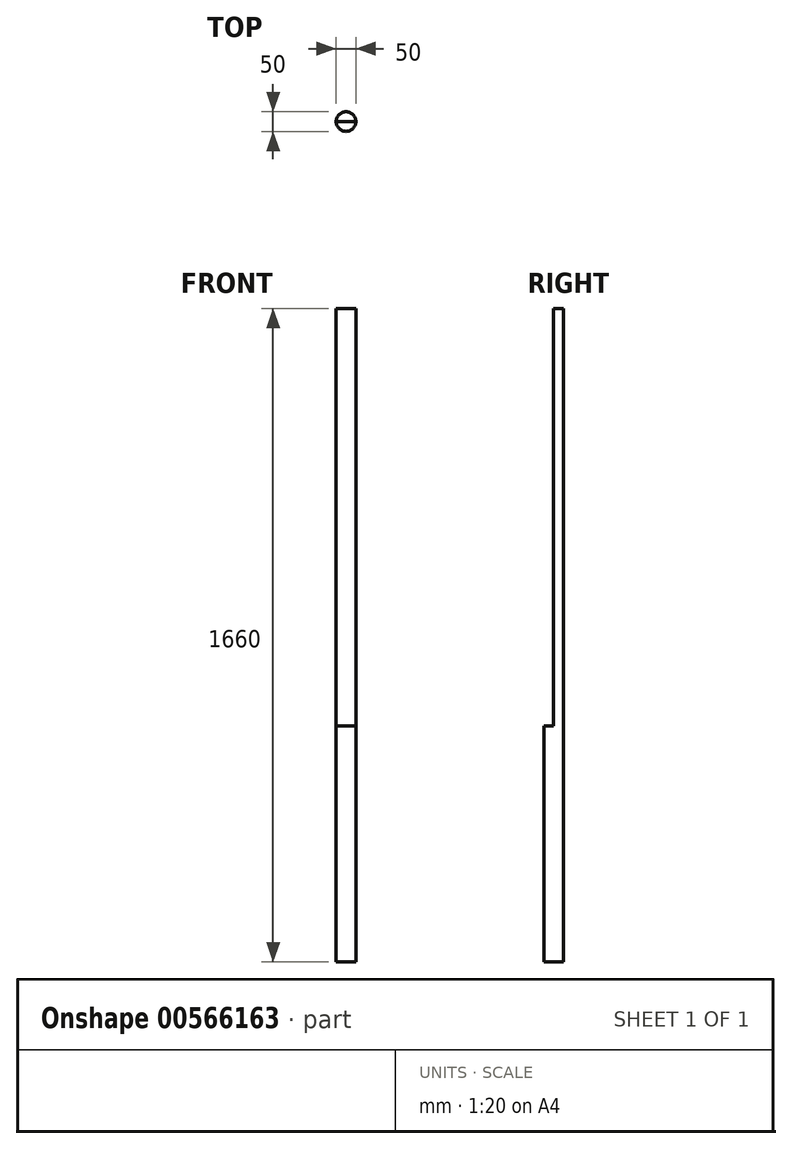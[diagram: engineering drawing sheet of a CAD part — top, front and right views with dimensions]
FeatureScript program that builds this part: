
annotation { "Feature Type Name" : "Feature", "Feature Type Description" : "" }
export const myFeature = defineFeature(function(context is Context, id is Id, definition is map)
    precondition{}
    {
        {
            var Q0;
            Q0=qCreatedBy(makeId("Top.planeOp"),FACE);
            var sketch = newSketch(context, id + "F0", { "sketchPlane" : qUnion([Q0])});
            skCircle(sketch, "E0", {"center": v(0, 0) * mm, "radius": 25 * mm});
            skLineSegment(sketch, "E1", {"start": v(-25, 0) * mm, "end": v(25, 0) * mm});
            skSolve(sketch);
        }
        {
            var Q0;
            {var subQ0=sQuery(id+"F0.wireOp",EDGE,"E1");Q0=makeQuery(id+"F0.imprint","IMPRINT",FACE,{"disambiguationData":[TD([[makeQuery(id+"F0.imprint","IMPRINT",EDGE,{"derivedFrom":subQ0}),1.0]])]});}
            var Q1;
            {var subQ0=sQuery(id+"F0.wireOp",EDGE,"E1");Q1=makeQuery(id+"F0.imprint","IMPRINT",FACE,{"disambiguationData":[TD([[makeQuery(id+"F0.imprint","IMPRINT",EDGE,{"derivedFrom":subQ0}),-1.0]])]});}
            extrude(context, id + "F1", {"entities" : qUnion([Q0, Q1]), "oppositeDirection" : true, "depth" : 600 * mm, "offsetDistance" : 25 * mm});
        }
        {
            var Q0;
            {var subQ0=sQuery(id+"F0.wireOp",EDGE,"E1");Q0=makeQuery(id+"F0.imprint","IMPRINT",FACE,{"disambiguationData":[TD([[makeQuery(id+"F0.imprint","IMPRINT",EDGE,{"derivedFrom":subQ0}),1.0]])]});}
            extrude(context, id + "F2", {"entities" : qUnion([Q0]), "operationType" : NewBodyOperationType.ADD, "depth" : 1060 * mm, "offsetDistance" : 25 * mm});
        }
    });
